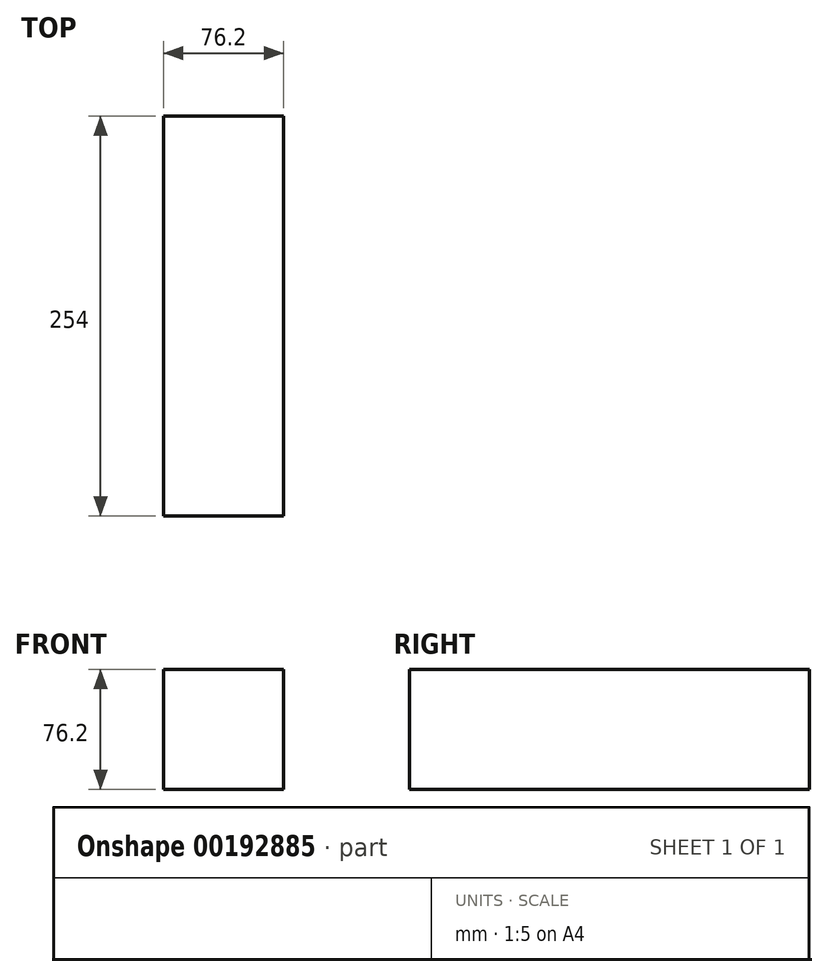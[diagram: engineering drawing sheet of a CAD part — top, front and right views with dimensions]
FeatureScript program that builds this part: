
annotation { "Feature Type Name" : "Feature", "Feature Type Description" : "" }
export const myFeature = defineFeature(function(context is Context, id is Id, definition is map)
    precondition{}
    {
        {
            var Q0;
            Q0=qCreatedBy(makeId("Front.planeOp"),FACE);
            var sketch = newSketch(context, id + "F0", { "sketchPlane" : qUnion([Q0])});
            skLineSegment(sketch, "E0.bottom", {"start": v(38.1, -38.1) * mm, "end": v(-38.1, -38.1) * mm});
            skLineSegment(sketch, "E0.top", {"start": v(38.1, 38.1) * mm, "end": v(-38.1, 38.1) * mm});
            skLineSegment(sketch, "E0.left", {"start": v(38.1, -38.1) * mm, "end": v(38.1, 38.1) * mm});
            skLineSegment(sketch, "E0.right", {"start": v(-38.1, -38.1) * mm, "end": v(-38.1, 38.1) * mm});
            skPoint(sketch, "E0.middle", {"position": v(0, 0) * mm});
            skSolve(sketch);
        }
        {
            var Q0;
            Q0=makeQuery(id+"F0.imprint","IMPRINT",FACE,{"disambiguationData":[TD([[makeQuery(id+"F0.imprint","IMPRINT",EDGE,{"derivedFrom":sQuery(id+"F0.wireOp",EDGE,"E0.bottom")}),-1.0]])]});
            extrude(context, id + "F1", {"entities" : qUnion([Q0]), "depth" : 254 * mm});
        }
    });
